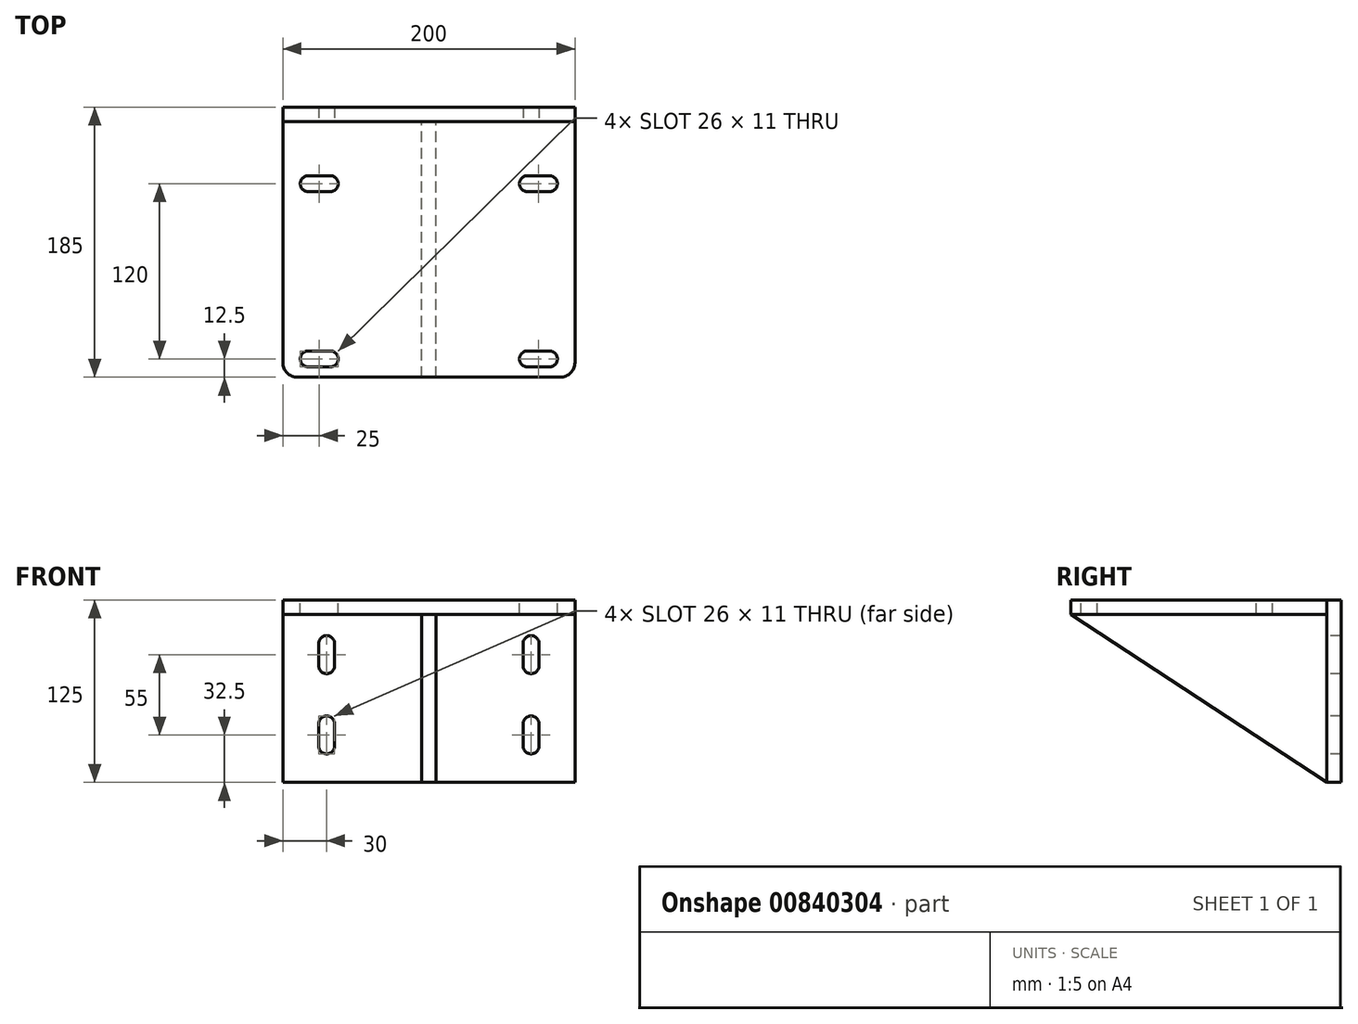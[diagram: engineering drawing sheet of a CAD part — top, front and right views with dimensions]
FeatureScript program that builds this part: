
annotation { "Feature Type Name" : "Feature", "Feature Type Description" : "" }
export const myFeature = defineFeature(function(context is Context, id is Id, definition is map)
    precondition{}
    {
        {
            var Q0;
            Q0=qCreatedBy(makeId("Front.planeOp"),FACE);
            var sketch = newSketch(context, id + "F0", { "sketchPlane" : qUnion([Q0])});
            skLineSegment(sketch, "E0.bottom", {"start": v(-100, -62.5) * mm, "end": v(100, -62.5) * mm});
            skLineSegment(sketch, "E0.top", {"start": v(-100, 62.5) * mm, "end": v(100, 62.5) * mm});
            skLineSegment(sketch, "E0.left", {"start": v(-100, -62.5) * mm, "end": v(-100, 62.5) * mm});
            skLineSegment(sketch, "E0.right", {"start": v(100, -62.5) * mm, "end": v(100, 62.5) * mm});
            skPoint(sketch, "E0.middle", {"position": v(0, 0) * mm});
            skSolve(sketch);
        }
        {
            var Q0;
            Q0 = qSketchRegion(id + "F0", true);
            extrude(context, id + "F1", {"entities" : qUnion([Q0]), "endBound" : BoundingType.SYMMETRIC, "depth" : 10 * mm, "offsetDistance" : 25 * mm});
        }
        {
            var Q0;
            Q0=makeQuery(id+"F1.opExtrude","CAP_FACE",FACE,{"disambiguationData":[OSD([sQuery(id+"F0.wireOp",EDGE,"E0.bottom"),sQuery(id+"F0.wireOp",EDGE,"E0.top"),sQuery(id+"F0.wireOp",EDGE,"E0.left"),sQuery(id+"F0.wireOp",EDGE,"E0.right")])],"isStart":false});
            var sketch = newSketch(context, id + "F2", { "sketchPlane" : qUnion([Q0])});
            skLineSegment(sketch, "E1.bottom", {"start": v(-100, 62.5) * mm, "end": v(100, 62.5) * mm});
            skLineSegment(sketch, "E1.top", {"start": v(-100, 52.5) * mm, "end": v(100, 52.5) * mm});
            skLineSegment(sketch, "E1.left", {"start": v(-100, 62.5) * mm, "end": v(-100, 52.5) * mm});
            skLineSegment(sketch, "E1.right", {"start": v(100, 62.5) * mm, "end": v(100, 52.5) * mm});
            skSolve(sketch);
        }
        {
            var Q0;
            Q0 = qSketchRegion(id + "F2", true);
            extrude(context, id + "F3", {"entities" : qUnion([Q0]), "depth" : 175 * mm, "offsetDistance" : 25 * mm});
        }
        {
            var Q0;
            Q0=makeQuery(id+"F1.opExtrude","CAP_FACE",FACE,{"disambiguationData":[OSD([sQuery(id+"F0.wireOp",EDGE,"E0.bottom"),sQuery(id+"F0.wireOp",EDGE,"E0.top"),sQuery(id+"F0.wireOp",EDGE,"E0.left"),sQuery(id+"F0.wireOp",EDGE,"E0.right")])],"isStart":false});
            var sketch = newSketch(context, id + "F4", { "sketchPlane" : qUnion([Q0])});
            skLineSegment(sketch, "E2", {"start": v(-70, 32.5) * mm, "end": v(-70, 17.5) * mm});
            skLineSegment(sketch, "E3", {"start": v(-70, -22.5) * mm, "end": v(-70, -37.5) * mm});
            skArc(sketch, "E4.0.startCap", {"start": v(-75.5, 32.5) * mm, "mid": v(-70, 38) * mm, "end": v(-64.5, 32.5) * mm});
            skArc(sketch, "E4.0.endCap", {"start": v(-64.5, 17.5) * mm, "mid": v(-70, 12) * mm, "end": v(-75.5, 17.5) * mm});
            skLineSegment(sketch, "E4.0.left", {"start": v(-64.5, 32.5) * mm, "end": v(-64.5, 17.5) * mm});
            skLineSegment(sketch, "E4.0.right", {"start": v(-75.5, 32.5) * mm, "end": v(-75.5, 17.5) * mm});
            skArc(sketch, "E4.1.startCap", {"start": v(-75.5, -22.5) * mm, "mid": v(-70, -17) * mm, "end": v(-64.5, -22.5) * mm});
            skArc(sketch, "E4.1.endCap", {"start": v(-64.5, -37.5) * mm, "mid": v(-70, -43) * mm, "end": v(-75.5, -37.5) * mm});
            skLineSegment(sketch, "E4.1.left", {"start": v(-64.5, -22.5) * mm, "end": v(-64.5, -37.5) * mm});
            skLineSegment(sketch, "E4.1.right", {"start": v(-75.5, -22.5) * mm, "end": v(-75.5, -37.5) * mm});
            skLineSegment(sketch, "E5.MirrorCS", {"start": v(64.5, 32.5) * mm, "end": v(64.5, 17.5) * mm});
            skArc(sketch, "E6.MirrorCS", {"start": v(75.5, 32.5) * mm, "mid": v(70, 38) * mm, "end": v(64.5, 32.5) * mm});
            skLineSegment(sketch, "E7.MirrorCS", {"start": v(75.5, 32.5) * mm, "end": v(75.5, 17.5) * mm});
            skArc(sketch, "E8.MirrorCS", {"start": v(64.5, 17.5) * mm, "mid": v(70, 12) * mm, "end": v(75.5, 17.5) * mm});
            skArc(sketch, "E9.MirrorCS", {"start": v(75.5, -22.5) * mm, "mid": v(70, -17) * mm, "end": v(64.5, -22.5) * mm});
            skLineSegment(sketch, "E10.MirrorCS", {"start": v(64.5, -22.5) * mm, "end": v(64.5, -37.5) * mm});
            skArc(sketch, "E11.MirrorCS", {"start": v(64.5, -37.5) * mm, "mid": v(70, -43) * mm, "end": v(75.5, -37.5) * mm});
            skLineSegment(sketch, "E12.MirrorCS", {"start": v(75.5, -22.5) * mm, "end": v(75.5, -37.5) * mm});
            skSolve(sketch);
        }
        {
            var Q0;
            Q0 = qSketchRegion(id + "F4", true);
            extrude(context, id + "F5", {"entities" : qUnion([Q0]), "operationType" : NewBodyOperationType.REMOVE, "endBound" : BoundingType.THROUGH_ALL, "oppositeDirection" : true, "depth" : 25 * mm, "offsetDistance" : 25 * mm});
        }
        {
            var Q0;
            Q0=qCreatedBy(makeId("Right.planeOp"),FACE);
            var sketch = newSketch(context, id + "F6", { "sketchPlane" : qUnion([Q0])});
            skLineSegment(sketch, "E13", {"start": v(-180, 52.5) * mm, "end": v(-5, 52.5) * mm});
            skLineSegment(sketch, "E14", {"start": v(-5, 52.5) * mm, "end": v(-5, -62.5) * mm});
            skLineSegment(sketch, "E15", {"start": v(-5, -62.5) * mm, "end": v(-180, 52.5) * mm});
            skSolve(sketch);
        }
        {
            var Q0;
            Q0=makeQuery(id+"F6.imprint","IMPRINT",FACE,{"disambiguationData":[TD([[makeQuery(id+"F6.imprint","IMPRINT",EDGE,{"derivedFrom":sQuery(id+"F6.wireOp",EDGE,"E13")}),-1.0]])]});
            extrude(context, id + "F7", {"entities" : qUnion([Q0]), "endBound" : BoundingType.SYMMETRIC, "depth" : 10 * mm, "offsetDistance" : 25 * mm});
        }
        {
            var Q0;
            Q0=makeQuery(id+"F3.opExtrude","SWEPT_FACE",FACE,{"disambiguationData":[OSD([sQuery(id+"F2.wireOp",EDGE,"E1.bottom")])]});
            var sketch = newSketch(context, id + "F8", { "sketchPlane" : qUnion([Q0])});
            skPoint(sketch, "E16", {"position": v(-75, -167.5) * mm});
            skPoint(sketch, "E17", {"position": v(75, -167.5) * mm});
            skPoint(sketch, "E18", {"position": v(75, -47.5) * mm});
            skPoint(sketch, "E19", {"position": v(-75, -47.5) * mm});
            skLineSegment(sketch, "E20", {"start": v(67.5, -47.5) * mm, "end": v(82.5, -47.5) * mm});
            skArc(sketch, "E21.0.startCap", {"start": v(67.5, -53) * mm, "mid": v(62, -47.5) * mm, "end": v(67.5, -42) * mm});
            skArc(sketch, "E21.0.endCap", {"start": v(82.5, -42) * mm, "mid": v(88, -47.5) * mm, "end": v(82.5, -53) * mm});
            skLineSegment(sketch, "E21.0.left", {"start": v(67.5, -42) * mm, "end": v(82.5, -42) * mm});
            skLineSegment(sketch, "E21.0.right", {"start": v(67.5, -53) * mm, "end": v(82.5, -53) * mm});
            skLineSegment(sketch, "E22", {"start": v(67.5, -167.5) * mm, "end": v(82.5, -167.5) * mm});
            skArc(sketch, "E23.0.startCap", {"start": v(67.5, -173) * mm, "mid": v(62, -167.5) * mm, "end": v(67.5, -162) * mm});
            skArc(sketch, "E23.0.endCap", {"start": v(82.5, -162) * mm, "mid": v(88, -167.5) * mm, "end": v(82.5, -173) * mm});
            skLineSegment(sketch, "E23.0.left", {"start": v(67.5, -162) * mm, "end": v(82.5, -162) * mm});
            skLineSegment(sketch, "E23.0.right", {"start": v(67.5, -173) * mm, "end": v(82.5, -173) * mm});
            skLineSegment(sketch, "E24.MirrorCS", {"start": v(-67.5, -47.5) * mm, "end": v(-82.5, -47.5) * mm});
            skLineSegment(sketch, "E25.MirrorCS", {"start": v(-67.5, -53) * mm, "end": v(-82.5, -53) * mm});
            skArc(sketch, "E26.MirrorCS", {"start": v(-67.5, -53) * mm, "mid": v(-62, -47.5) * mm, "end": v(-67.5, -42) * mm});
            skArc(sketch, "E27.MirrorCS", {"start": v(-82.5, -42) * mm, "mid": v(-88, -47.5) * mm, "end": v(-82.5, -53) * mm});
            skLineSegment(sketch, "E28.MirrorCS", {"start": v(-67.5, -42) * mm, "end": v(-82.5, -42) * mm});
            skLineSegment(sketch, "E29.MirrorCS", {"start": v(-67.5, -167.5) * mm, "end": v(-82.5, -167.5) * mm});
            skLineSegment(sketch, "E30.MirrorCS", {"start": v(-67.5, -173) * mm, "end": v(-82.5, -173) * mm});
            skArc(sketch, "E31.MirrorCS", {"start": v(-82.5, -162) * mm, "mid": v(-88, -167.5) * mm, "end": v(-82.5, -173) * mm});
            skLineSegment(sketch, "E32.MirrorCS", {"start": v(-67.5, -162) * mm, "end": v(-82.5, -162) * mm});
            skArc(sketch, "E33.MirrorCS", {"start": v(-67.5, -173) * mm, "mid": v(-62, -167.5) * mm, "end": v(-67.5, -162) * mm});
            skSolve(sketch);
        }
        {
            var Q0;
            Q0 = qSketchRegion(id + "F8", true);
            extrude(context, id + "F9", {"entities" : qUnion([Q0]), "operationType" : NewBodyOperationType.REMOVE, "endBound" : BoundingType.THROUGH_ALL, "oppositeDirection" : true, "depth" : 25 * mm, "offsetDistance" : 25 * mm});
        }
        {
            var Q0;
            Q0=makeQuery(id+"F3.opExtrude","CAP_EDGE",EDGE,{"disambiguationData":[OSD([sQuery(id+"F2.wireOp",EDGE,"E1.right")])],"isStart":false});
            var Q1;
            Q1=makeQuery(id+"F3.opExtrude","CAP_EDGE",EDGE,{"disambiguationData":[OSD([sQuery(id+"F2.wireOp",EDGE,"E1.left")])],"isStart":false});
            fillet(context, id + "F10", {"entities" : qUnion([Q0, Q1]), "radius" : 10 * mm, "tangentPropagation" : true, "allowEdgeOverflow" : false});
        }
    });
